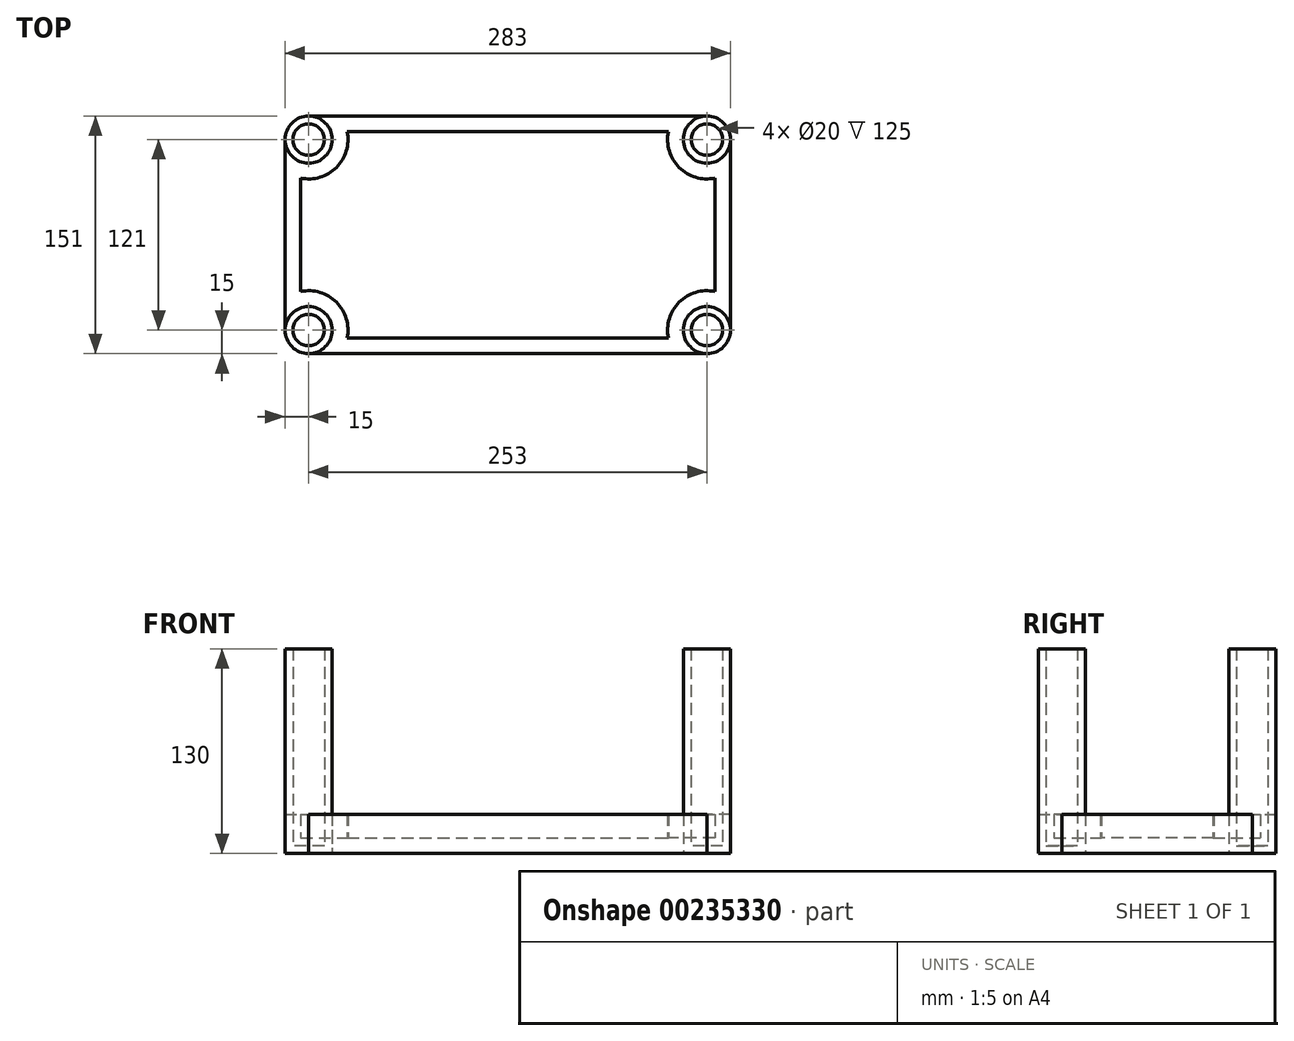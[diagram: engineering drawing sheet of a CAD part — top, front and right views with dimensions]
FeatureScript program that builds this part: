
annotation { "Feature Type Name" : "Feature", "Feature Type Description" : "" }
export const myFeature = defineFeature(function(context is Context, id is Id, definition is map)
    precondition{}
    {
        {
            var Q0;
            Q0=qCreatedBy(makeId("Top.planeOp"),FACE);
            var sketch = newSketch(context, id + "F0", { "sketchPlane" : qUnion([Q0])});
            skLineSegment(sketch, "E0.bottom", {"start": v(0, 0) * mm, "end": v(283, 0) * mm});
            skLineSegment(sketch, "E0.top", {"start": v(0, -151) * mm, "end": v(283, -151) * mm});
            skLineSegment(sketch, "E0.left", {"start": v(0, 0) * mm, "end": v(0, -151) * mm});
            skLineSegment(sketch, "E0.right", {"start": v(283, 0) * mm, "end": v(283, -151) * mm});
            skCircle(sketch, "E1", {"center": v(15, -136) * mm, "radius": 15 * mm});
            skCircle(sketch, "E2", {"center": v(15, -15) * mm, "radius": 15 * mm});
            skCircle(sketch, "E3", {"center": v(268, -15) * mm, "radius": 15 * mm});
            skCircle(sketch, "E4", {"center": v(268, -136) * mm, "radius": 15 * mm});
            skSolve(sketch);
        }
        {
            var Q0;
            {var subQ5=sQuery(id+"F0.wireOp",EDGE,"E2");var subQ13=sQuery(id+"F0.wireOp",EDGE,"E0.bottom");var subQ14=makeQuery(id+"F0.imprint","INTERSECT",VERTEX,{"derivedFrom":[subQ13,subQ5]});Q0=makeQuery(id+"F0.imprint","IMPRINT",FACE,{"disambiguationData":[TD([[makeQuery(id+"F0.imprint","IMPRINT",EDGE,{"disambiguationData":[TD([[subQ14,-1.0]])],"derivedFrom":subQ13}),-1.0]])]});}
            extrude(context, id + "F1", {"entities" : qUnion([Q0]), "depth" : 25 * mm});
        }
        {
            var Q0;
            {var subQ0=sQuery(id+"F0.wireOp",EDGE,"E2");var subQ1=makeQuery(id+"F0.imprint","INTERSECT",VERTEX,{"derivedFrom":[sQuery(id+"F0.wireOp",EDGE,"E0.bottom"),subQ0]});Q0=makeQuery(id+"F0.imprint","IMPRINT",FACE,{"disambiguationData":[TD([[makeQuery(id+"F0.imprint","IMPRINT",EDGE,{"disambiguationData":[TD([[subQ1,-1.0]])],"derivedFrom":subQ0}),1.0]])]});}
            var Q1;
            {var subQ0=sQuery(id+"F0.wireOp",EDGE,"E1");var subQ1=makeQuery(id+"F0.imprint","INTERSECT",VERTEX,{"derivedFrom":[sQuery(id+"F0.wireOp",EDGE,"E0.top"),subQ0]});Q1=makeQuery(id+"F0.imprint","IMPRINT",FACE,{"disambiguationData":[TD([[makeQuery(id+"F0.imprint","IMPRINT",EDGE,{"disambiguationData":[TD([[subQ1,1.0]])],"derivedFrom":subQ0}),1.0]])]});}
            var Q2;
            {var subQ0=sQuery(id+"F0.wireOp",EDGE,"E4");var subQ1=makeQuery(id+"F0.imprint","INTERSECT",VERTEX,{"derivedFrom":[sQuery(id+"F0.wireOp",EDGE,"E0.top"),subQ0]});Q2=makeQuery(id+"F0.imprint","IMPRINT",FACE,{"disambiguationData":[TD([[makeQuery(id+"F0.imprint","IMPRINT",EDGE,{"disambiguationData":[TD([[subQ1,1.0]])],"derivedFrom":subQ0}),1.0]])]});}
            var Q3;
            {var subQ0=sQuery(id+"F0.wireOp",EDGE,"E3");var subQ1=makeQuery(id+"F0.imprint","INTERSECT",VERTEX,{"derivedFrom":[sQuery(id+"F0.wireOp",EDGE,"E0.bottom"),subQ0]});Q3=makeQuery(id+"F0.imprint","IMPRINT",FACE,{"disambiguationData":[TD([[makeQuery(id+"F0.imprint","IMPRINT",EDGE,{"disambiguationData":[TD([[subQ1,1.0]])],"derivedFrom":subQ0}),1.0]])]});}
            extrude(context, id + "F2", {"entities" : qUnion([Q0, Q1, Q2, Q3]), "depth" : 130 * mm});
        }
        {
            var Q0;
            Q0=makeQuery(id+"F1.opExtrude","CAP_FACE",FACE,{"disambiguationData":[OSD([sQuery(id+"F0.wireOp",EDGE,"E0.bottom"),sQuery(id+"F0.wireOp",EDGE,"E0.top"),sQuery(id+"F0.wireOp",EDGE,"E0.left"),sQuery(id+"F0.wireOp",EDGE,"E0.right"),sQuery(id+"F0.wireOp",EDGE,"E1"),sQuery(id+"F0.wireOp",EDGE,"E2"),sQuery(id+"F0.wireOp",EDGE,"E3"),sQuery(id+"F0.wireOp",EDGE,"E4")])],"isStart":false});
            shell(context, id + "F3", {"entities" : qUnion([Q0]), "thickness" : 10 * mm});
        }
        {
            var Q0;
            Q0=makeQuery(id+"F2.opExtrude","CAP_FACE",FACE,{"disambiguationData":[OSD([sQuery(id+"F0.wireOp",EDGE,"E2")])],"isStart":false});
            var Q1;
            Q1=makeQuery(id+"F2.opExtrude","CAP_FACE",FACE,{"disambiguationData":[OSD([sQuery(id+"F0.wireOp",EDGE,"E1")])],"isStart":false});
            var Q2;
            Q2=makeQuery(id+"F2.opExtrude","CAP_FACE",FACE,{"disambiguationData":[OSD([sQuery(id+"F0.wireOp",EDGE,"E4")])],"isStart":false});
            var Q3;
            Q3=makeQuery(id+"F2.opExtrude","CAP_FACE",FACE,{"disambiguationData":[OSD([sQuery(id+"F0.wireOp",EDGE,"E3")])],"isStart":false});
            shell(context, id + "F4", {"entities" : qUnion([Q0, Q1, Q2, Q3]), "thickness" : 5 * mm});
        }
    });
